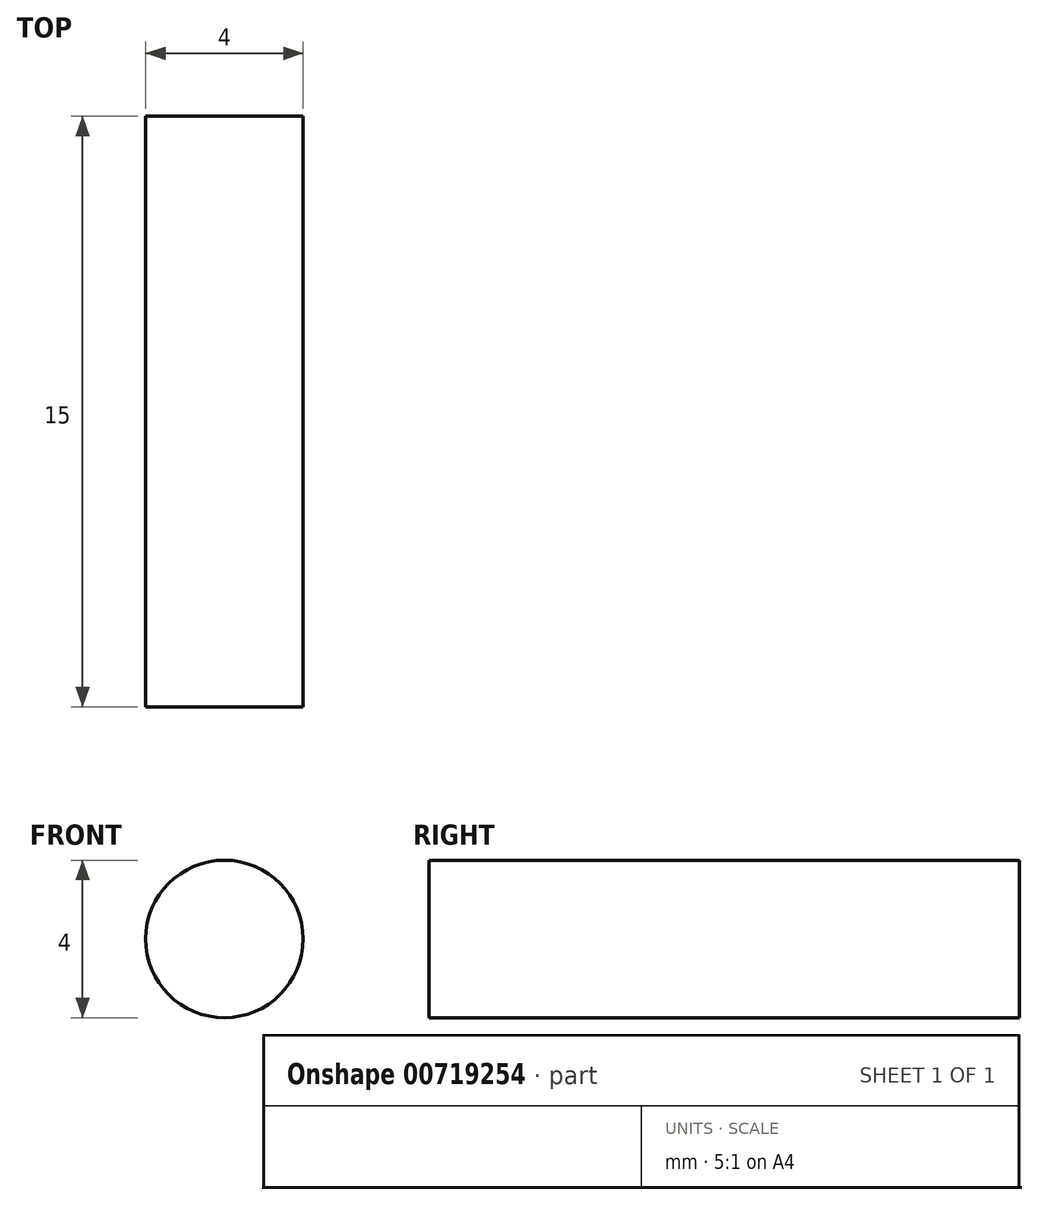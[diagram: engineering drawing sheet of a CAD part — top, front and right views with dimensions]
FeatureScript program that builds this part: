
annotation { "Feature Type Name" : "Feature", "Feature Type Description" : "" }
export const myFeature = defineFeature(function(context is Context, id is Id, definition is map)
    precondition{}
    {
        {
            var Q0;
            Q0=qCreatedBy(makeId("Front.planeOp"),FACE);
            var sketch = newSketch(context, id + "F0", { "sketchPlane" : qUnion([Q0])});
            skCircle(sketch, "E0", {"center": v(0, 0) * mm, "radius": 2 * mm});
            skSolve(sketch);
        }
        {
            var Q0;
            Q0 = qSketchRegion(id + "F0", true);
            extrude(context, id + "F1", {"entities" : qUnion([Q0]), "depth" : 15 * mm, "offsetDistance" : 25.4 * mm});
        }
    });
